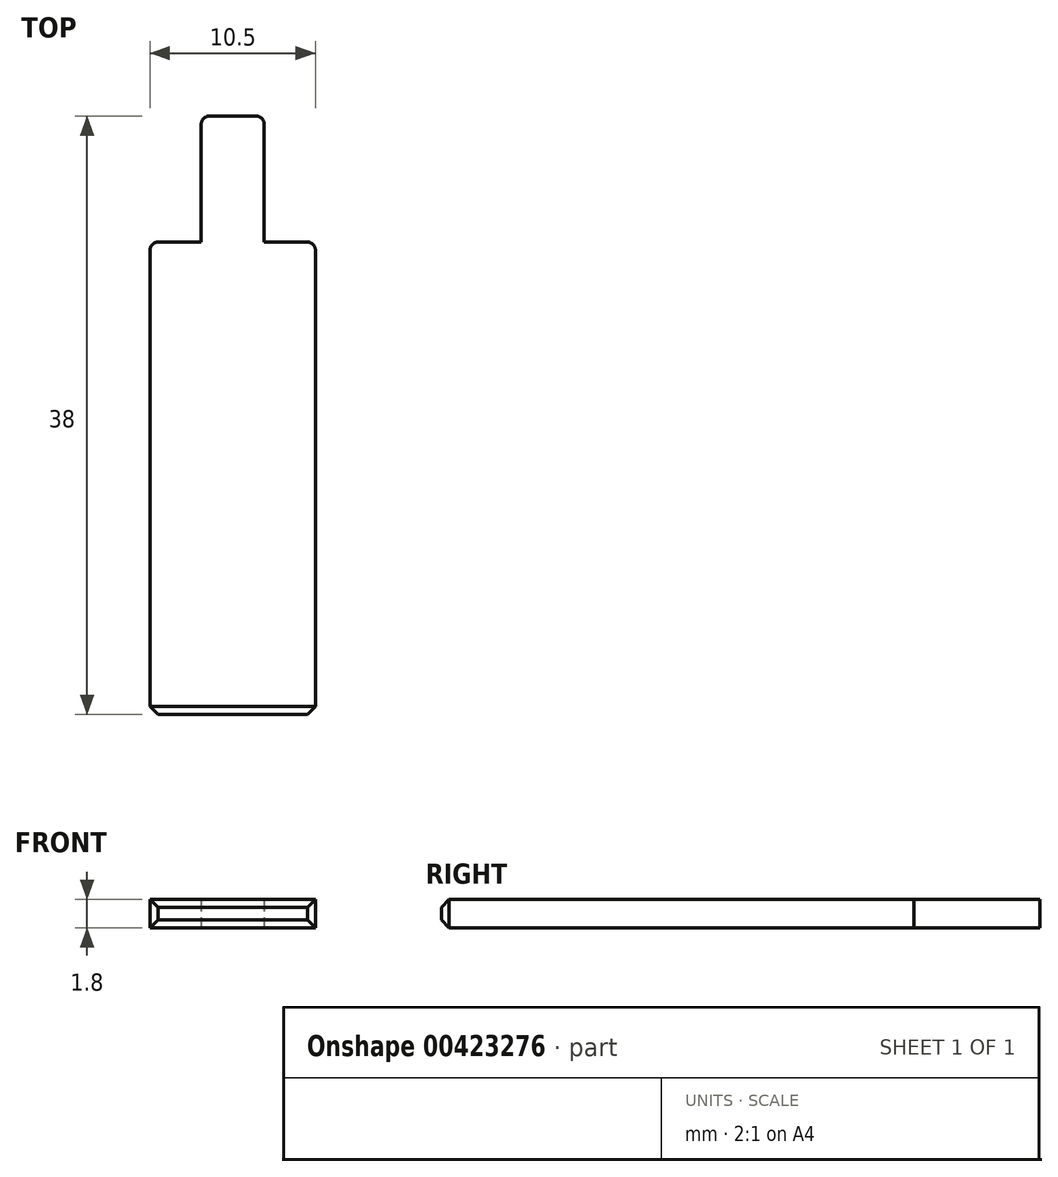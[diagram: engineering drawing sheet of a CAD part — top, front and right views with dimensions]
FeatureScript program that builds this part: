
annotation { "Feature Type Name" : "Feature", "Feature Type Description" : "" }
export const myFeature = defineFeature(function(context is Context, id is Id, definition is map)
    precondition{}
    {
        {
            var Q0;
            Q0=qCreatedBy(makeId("Top.planeOp"),FACE);
            var sketch = newSketch(context, id + "F0", { "sketchPlane" : qUnion([Q0])});
            skLineSegment(sketch, "E0.bottom", {"start": v(5.25, -15) * mm, "end": v(-5.25, -15) * mm});
            skLineSegment(sketch, "E0.top", {"start": v(5.25, 15) * mm, "end": v(2, 15) * mm});
            skLineSegment(sketch, "E0.left", {"start": v(5.25, -15) * mm, "end": v(5.25, 15) * mm});
            skLineSegment(sketch, "E0.right", {"start": v(-5.25, -15) * mm, "end": v(-5.25, 15) * mm});
            skPoint(sketch, "E0.middle", {"position": v(0, 0) * mm});
            skLineSegment(sketch, "E1", {"start": v(0, 0) * mm, "end": v(0, 32.93) * mm, "construction": true});
            skPoint(sketch, "E1.endSnap0", {"position": v(0, 15) * mm});
            skLineSegment(sketch, "E2", {"start": v(-2, 15) * mm, "end": v(-2, 23) * mm});
            skLineSegment(sketch, "E3", {"start": v(-2, 23) * mm, "end": v(0, 23) * mm});
            skLineSegment(sketch, "E4.MirrorCS", {"start": v(2, 23) * mm, "end": v(0, 23) * mm});
            skLineSegment(sketch, "E5.MirrorCS", {"start": v(2, 15) * mm, "end": v(2, 23) * mm});
            skLineSegment(sketch, "E6.trimOffspring", {"start": v(-2, 15) * mm, "end": v(-5.25, 15) * mm});
            skSolve(sketch);
        }
        {
            var Q0;
            Q0 = qSketchRegion(id + "F0", true);
            extrude(context, id + "F1", {"entities" : qUnion([Q0]), "depth" : 1.8 * mm});
        }
        {
            var Q0;
            Q0=makeQuery(id+"F1.opExtrude","SWEPT_EDGE",EDGE,{"disambiguationData":[OSD([sQuery(id+"F0.wireOp",EDGE,"E4.MirrorCS"),sQuery(id+"F0.wireOp",EDGE,"E5.MirrorCS")])]});
            var Q1;
            Q1=makeQuery(id+"F1.opExtrude","SWEPT_EDGE",EDGE,{"disambiguationData":[OSD([sQuery(id+"F0.wireOp",EDGE,"E2"),sQuery(id+"F0.wireOp",EDGE,"E3")])]});
            var Q2;
            Q2=makeQuery(id+"F1.opExtrude","SWEPT_EDGE",EDGE,{"disambiguationData":[OSD([sQuery(id+"F0.wireOp",EDGE,"E0.top"),sQuery(id+"F0.wireOp",EDGE,"E0.left")])]});
            var Q3;
            Q3=makeQuery(id+"F1.opExtrude","SWEPT_EDGE",EDGE,{"disambiguationData":[OSD([sQuery(id+"F0.wireOp",EDGE,"E0.right"),sQuery(id+"F0.wireOp",EDGE,"E6.trimOffspring")])]});
            fillet(context, id + "F2", {"entities" : qUnion([Q0, Q1, Q2, Q3]), "radius" : 0.5 * mm, "tangentPropagation" : true, "allowEdgeOverflow" : false});
        }
        {
            var Q0;
            Q0=makeQuery(id+"F1.opExtrude","CAP_EDGE",EDGE,{"disambiguationData":[OSD([sQuery(id+"F0.wireOp",EDGE,"E0.bottom")])],"isStart":true});
            var Q1;
            Q1=makeQuery(id+"F1.opExtrude","CAP_EDGE",EDGE,{"disambiguationData":[OSD([sQuery(id+"F0.wireOp",EDGE,"E0.bottom")])],"isStart":false});
            var Q2;
            Q2=makeQuery(id+"F1.opExtrude","SWEPT_EDGE",EDGE,{"disambiguationData":[OSD([sQuery(id+"F0.wireOp",EDGE,"E0.bottom"),sQuery(id+"F0.wireOp",EDGE,"E0.left")])]});
            var Q3;
            Q3=makeQuery(id+"F1.opExtrude","SWEPT_EDGE",EDGE,{"disambiguationData":[OSD([sQuery(id+"F0.wireOp",EDGE,"E0.bottom"),sQuery(id+"F0.wireOp",EDGE,"E0.right")])]});
            chamfer(context, id + "F3", {"entities" : qUnion([Q0, Q1, Q2, Q3]), "width" : 0.5 * mm, "tangentPropagation" : true});
        }
    });
